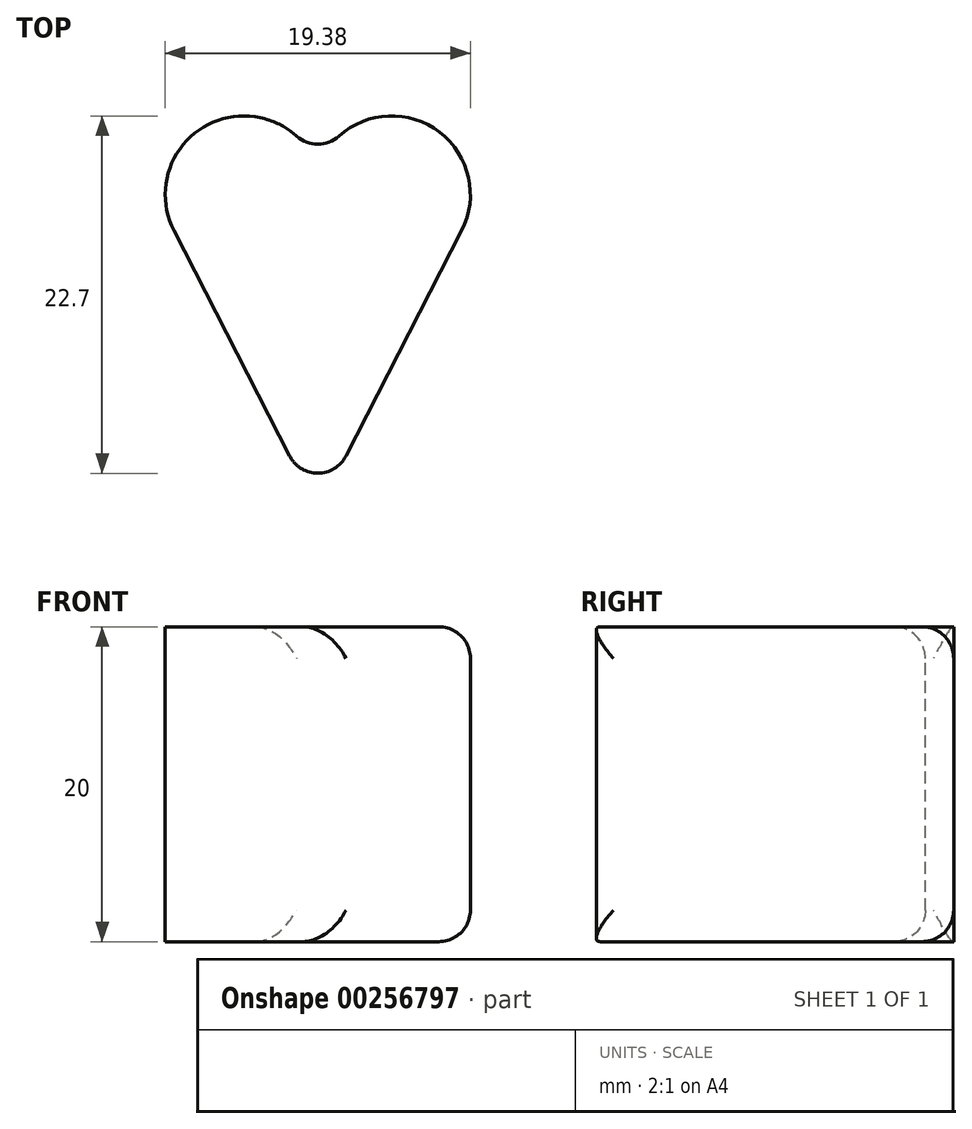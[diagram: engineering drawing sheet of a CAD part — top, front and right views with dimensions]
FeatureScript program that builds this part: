
annotation { "Feature Type Name" : "Feature", "Feature Type Description" : "" }
export const myFeature = defineFeature(function(context is Context, id is Id, definition is map)
    precondition{}
    {
        {
            var Q0;
            Q0=qCreatedBy(makeId("Top.planeOp"),FACE);
            var sketch = newSketch(context, id + "F0", { "sketchPlane" : qUnion([Q0])});
            skLineSegment(sketch, "E0", {"start": v(-9.14, -0.55) * mm, "end": v(0, -18.34) * mm});
            skArc(sketch, "E1", {"start": v(0, 0) * mm, "mid": v(-4.99, 6.73) * mm, "end": v(-9.14, -0.55) * mm});
            skArc(sketch, "E2.MirrorCS", {"start": v(0, 0) * mm, "mid": v(4.99, 6.73) * mm, "end": v(9.14, -0.55) * mm});
            skLineSegment(sketch, "E3.MirrorCS", {"start": v(9.14, -0.55) * mm, "end": v(0, -18.34) * mm});
            skSolve(sketch);
        }
        {
            var Q0;
            Q0=qSketchRegion(id+"F0",true);
            extrude(context, id + "F1", {"entities" : qUnion([Q0]), "depth" : 20 * mm});
        }
        {
            var Q0;
            Q0=makeQuery(id+"F1.opExtrude","SWEPT_FACE",FACE,{"disambiguationData":[OSD([sQuery(id+"F0.wireOp",EDGE,"E2.MirrorCS")])]});
            var Q1;
            Q1=makeQuery(id+"F1.opExtrude","SWEPT_FACE",FACE,{"disambiguationData":[OSD([sQuery(id+"F0.wireOp",EDGE,"E3.MirrorCS")])]});
            fillet(context, id + "F2", {"entities" : qUnion([Q0, Q1]), "radius" : 2 * mm, "tangentPropagation" : true, "allowEdgeOverflow" : false});
        }
    });
